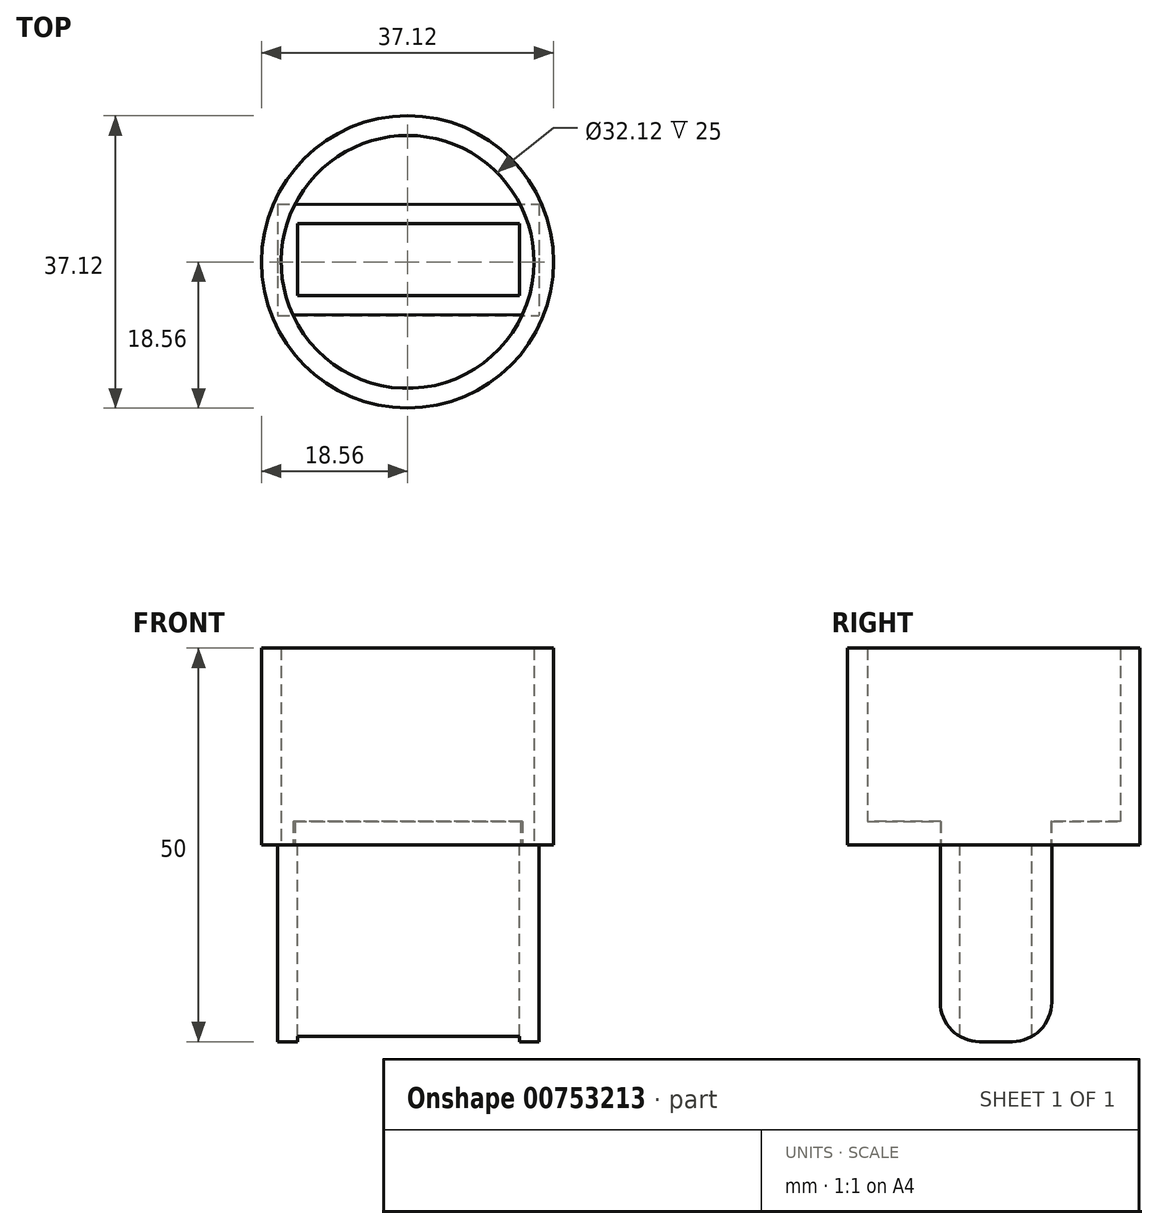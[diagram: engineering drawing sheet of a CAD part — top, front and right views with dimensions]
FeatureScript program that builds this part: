
annotation { "Feature Type Name" : "Feature", "Feature Type Description" : "" }
export const myFeature = defineFeature(function(context is Context, id is Id, definition is map)
    precondition{}
    {
        {
            var Q0;
            Q0=qCreatedBy(makeId("Top.planeOp"),FACE);
            var sketch = newSketch(context, id + "F0", { "sketchPlane" : qUnion([Q0])});
            skCircle(sketch, "E0", {"center": v(0, 0) * mm, "radius": 18.56 * mm});
            skSolve(sketch);
        }
        {
            var Q0;
            Q0=makeQuery(id+"F0.imprint","IMPRINT",FACE,{"disambiguationData":[TD([[makeQuery(id+"F0.imprint","IMPRINT",EDGE,{"derivedFrom":sQuery(id+"F0.wireOp",EDGE,"E0")}),1.0]])]});
            extrude(context, id + "F1", {"entities" : qUnion([Q0]), "depth" : 25 * mm, "offsetDistance" : 25 * mm});
        }
        {
            var Q0;
            Q0=makeQuery(id+"F1.opExtrude","CAP_FACE",FACE,{"disambiguationData":[OSD([sQuery(id+"F0.wireOp",EDGE,"E0")])],"isStart":false});
            var Q1;
            Q1=makeQuery(id+"F1.opExtrude","CAP_FACE",FACE,{"disambiguationData":[OSD([sQuery(id+"F0.wireOp",EDGE,"E0")])],"isStart":true});
            shell(context, id + "F2", {"entities" : qUnion([Q0, Q1]), "thickness" : 2.5 * mm});
        }
        {
            var Q0;
            Q0=qCreatedBy(makeId("Top.planeOp"),FACE);
            var sketch = newSketch(context, id + "F3", { "sketchPlane" : qUnion([Q0])});
            skLineSegment(sketch, "E1.bottom", {"start": v(-16.5, 7.36) * mm, "end": v(16.7, 7.36) * mm});
            skLineSegment(sketch, "E1.top", {"start": v(-16.5, -6.8) * mm, "end": v(16.7, -6.8) * mm});
            skLineSegment(sketch, "E1.left", {"start": v(-16.5, 7.36) * mm, "end": v(-16.5, -6.8) * mm});
            skLineSegment(sketch, "E1.right", {"start": v(16.7, 7.36) * mm, "end": v(16.7, -6.8) * mm});
            skSolve(sketch);
        }
        {
            var Q0;
            Q0=makeQuery(id+"F3.imprint","IMPRINT",FACE,{"disambiguationData":[TD([[makeQuery(id+"F3.imprint","IMPRINT",EDGE,{"derivedFrom":sQuery(id+"F3.wireOp",EDGE,"E1.bottom")}),-1.0]])]});
            extrude(context, id + "F4", {"entities" : qUnion([Q0]), "operationType" : NewBodyOperationType.ADD, "oppositeDirection" : true, "depth" : 25 * mm, "offsetDistance" : 25 * mm});
        }
        {
            var Q0;
            Q0=makeQuery(id+"F4.opExtrude","CAP_FACE",FACE,{"disambiguationData":[OSD([sQuery(id+"F3.wireOp",EDGE,"E1.bottom"),sQuery(id+"F3.wireOp",EDGE,"E1.top"),sQuery(id+"F3.wireOp",EDGE,"E1.left"),sQuery(id+"F3.wireOp",EDGE,"E1.right")])],"isStart":false});
            var Q1;
            Q1=makeQuery(id+"F4.opExtrude","CAP_FACE",FACE,{"disambiguationData":[OSD([sQuery(id+"F3.wireOp",EDGE,"E1.bottom"),sQuery(id+"F3.wireOp",EDGE,"E1.top"),sQuery(id+"F3.wireOp",EDGE,"E1.left"),sQuery(id+"F3.wireOp",EDGE,"E1.right")])],"isStart":true});
            shell(context, id + "F5", {"entities" : qUnion([Q0, Q1]), "thickness" : 2.5 * mm});
        }
        {
            var Q0;
            Q0=qCreatedBy(makeId("Top.planeOp"),FACE);
            var sketch = newSketch(context, id + "F6", { "sketchPlane" : qUnion([Q0])});
            skArc(sketch, "E2", {"start": v(-16.56, -6.76) * mm, "mid": v(0.06, -17.87) * mm, "end": v(16.66, -6.72) * mm});
            skLineSegment(sketch, "E3", {"start": v(16.66, -6.72) * mm, "end": v(-16.56, -6.76) * mm});
            skSolve(sketch);
        }
        {
            var Q0;
            Q0=makeQuery(id+"F6.imprint","IMPRINT",FACE,{"disambiguationData":[TD([[makeQuery(id+"F6.imprint","IMPRINT",EDGE,{"derivedFrom":sQuery(id+"F6.wireOp",EDGE,"E2")}),1.0]])]});
            extrude(context, id + "F7", {"entities" : qUnion([Q0]), "operationType" : NewBodyOperationType.ADD, "depth" : 3 * mm, "offsetDistance" : 25 * mm});
        }
        {
            var Q0;
            Q0=qCreatedBy(makeId("Top.planeOp"),FACE);
            var sketch = newSketch(context, id + "F8", { "sketchPlane" : qUnion([Q0])});
            skArc(sketch, "E4", {"start": v(16.56, 7.28) * mm, "mid": v(0.09, 17.71) * mm, "end": v(-16.4, 7.31) * mm});
            skLineSegment(sketch, "E5", {"start": v(-16.4, 7.31) * mm, "end": v(16.56, 7.28) * mm});
            skSolve(sketch);
        }
        {
            var Q0;
            Q0=makeQuery(id+"F8.imprint","IMPRINT",FACE,{"disambiguationData":[TD([[makeQuery(id+"F8.imprint","IMPRINT",EDGE,{"derivedFrom":sQuery(id+"F8.wireOp",EDGE,"E4")}),1.0]])]});
            extrude(context, id + "F9", {"entities" : qUnion([Q0]), "operationType" : NewBodyOperationType.ADD, "depth" : 3 * mm, "offsetDistance" : 25 * mm});
        }
        {
            var Q0;
            Q0=makeQuery(id+"F4.opExtrude","CAP_EDGE",EDGE,{"disambiguationData":[OSD([sQuery(id+"F3.wireOp",EDGE,"E1.top")])],"isStart":false});
            fillet(context, id + "F10", {"entities" : qUnion([Q0]), "radius" : 5 * mm, "tangentPropagation" : true, "allowEdgeOverflow" : false});
        }
        {
            var Q0;
            Q0=makeQuery(id+"F4.opExtrude","CAP_EDGE",EDGE,{"disambiguationData":[OSD([sQuery(id+"F3.wireOp",EDGE,"E1.bottom")])],"isStart":false});
            fillet(context, id + "F11", {"entities" : qUnion([Q0]), "radius" : 5 * mm, "tangentPropagation" : true, "allowEdgeOverflow" : false});
        }
    });
